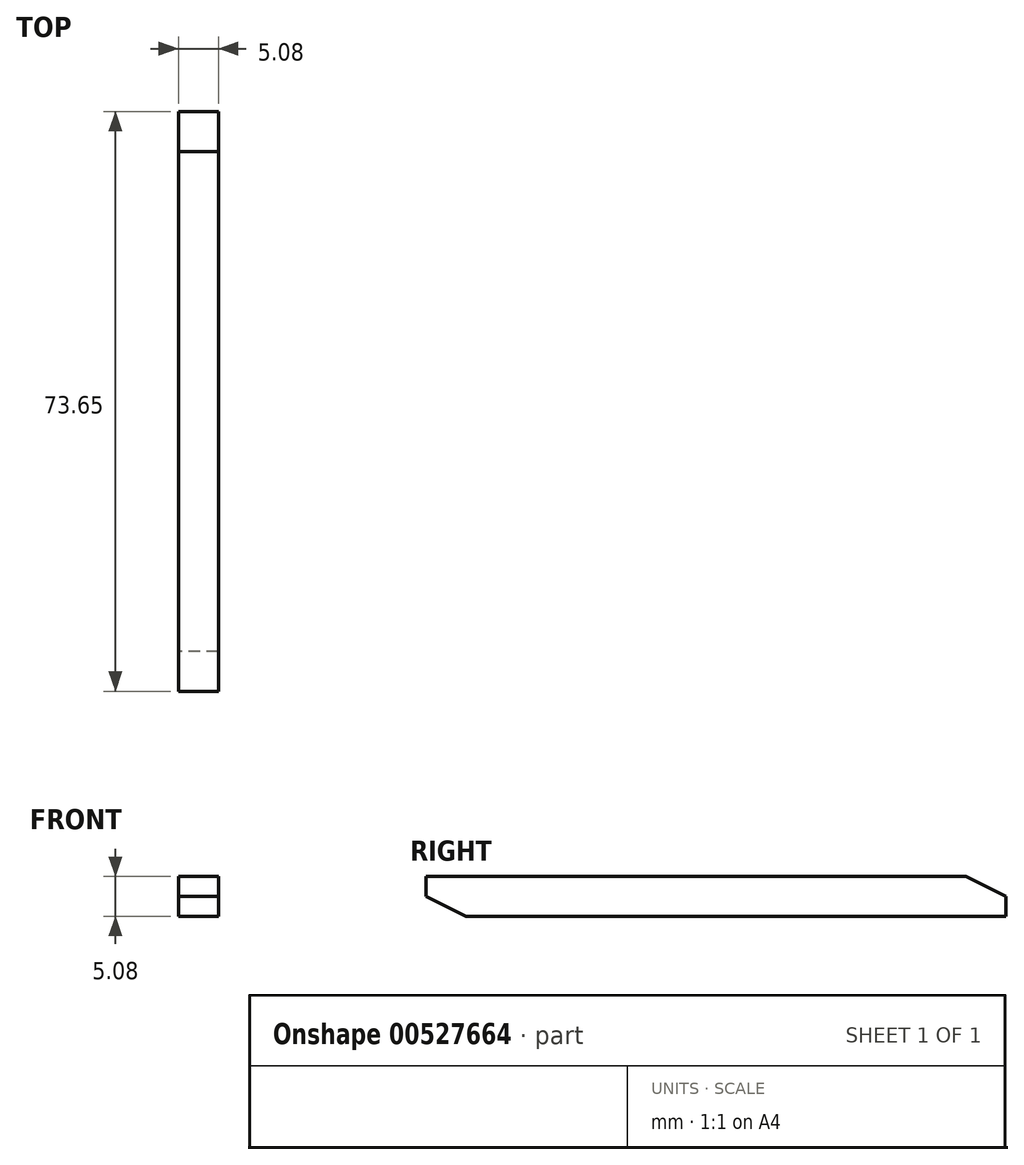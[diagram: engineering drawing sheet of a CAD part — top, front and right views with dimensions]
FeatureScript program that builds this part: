
annotation { "Feature Type Name" : "Feature", "Feature Type Description" : "" }
export const myFeature = defineFeature(function(context is Context, id is Id, definition is map)
    precondition{}
    {
        {
            var Q0;
            Q0=qCreatedBy(makeId("Right.planeOp"),FACE);
            var sketch = newSketch(context, id + "F0", { "sketchPlane" : qUnion([Q0])});
            skLineSegment(sketch, "E0.bottom", {"start": v(-23.9, 3.95) * mm, "end": v(39.6, 3.95) * mm});
            skLineSegment(sketch, "E0.top", {"start": v(-23.9, 9.03) * mm, "end": v(39.6, 9.03) * mm});
            skLineSegment(sketch, "E0.left", {"start": v(-23.9, 3.95) * mm, "end": v(-23.9, 9.03) * mm});
            skLineSegment(sketch, "E0.right", {"start": v(39.6, 3.95) * mm, "end": v(39.6, 9.03) * mm});
            skCircle(sketch, "E1.cCircle", {"center": v(-23.9, 6.5) * mm, "radius": 2.54 * mm, "construction": true});
            skLineSegment(sketch, "E1.0", {"start": v(-23.9, 3.95) * mm, "end": v(-26.44, 6.5) * mm});
            skLineSegment(sketch, "E1.1", {"start": v(-26.44, 6.5) * mm, "end": v(-23.9, 9.03) * mm});
            skLineSegment(sketch, "E1.2", {"start": v(-23.9, 9.03) * mm, "end": v(-21.36, 6.5) * mm});
            skLineSegment(sketch, "E1.3", {"start": v(-21.36, 6.5) * mm, "end": v(-23.9, 3.95) * mm});
            skLineSegment(sketch, "E2.bottom", {"start": v(-23.9, 9.03) * mm, "end": v(-28.98, 9.03) * mm});
            skLineSegment(sketch, "E2.top", {"start": v(-23.9, 6.5) * mm, "end": v(-28.98, 6.5) * mm});
            skLineSegment(sketch, "E2.left", {"start": v(-23.9, 9.03) * mm, "end": v(-23.9, 6.5) * mm});
            skLineSegment(sketch, "E2.right", {"start": v(-28.98, 9.03) * mm, "end": v(-28.98, 6.5) * mm});
            skLineSegment(sketch, "E3", {"start": v(-28.98, 6.5) * mm, "end": v(-23.9, 3.95) * mm});
            skLineSegment(sketch, "E4.bottom", {"start": v(39.6, 9.03) * mm, "end": v(39.6, 9.03) * mm});
            skLineSegment(sketch, "E4.top", {"start": v(39.6, 6.5) * mm, "end": v(39.6, 6.5) * mm});
            skLineSegment(sketch, "E4.left", {"start": v(39.6, 9.03) * mm, "end": v(39.6, 6.5) * mm});
            skLineSegment(sketch, "E4.right", {"start": v(39.6, 9.03) * mm, "end": v(39.6, 6.5) * mm});
            skLineSegment(sketch, "E5.bottom", {"start": v(39.6, 6.5) * mm, "end": v(44.67, 6.5) * mm});
            skLineSegment(sketch, "E5.left", {"start": v(39.6, 6.5) * mm, "end": v(39.6, 9.03) * mm});
            skLineSegment(sketch, "E6.bottom", {"start": v(44.67, 6.5) * mm, "end": v(39.6, 6.5) * mm});
            skLineSegment(sketch, "E6.top", {"start": v(44.67, 3.95) * mm, "end": v(39.6, 3.95) * mm});
            skLineSegment(sketch, "E6.left", {"start": v(44.67, 6.5) * mm, "end": v(44.67, 3.95) * mm});
            skLineSegment(sketch, "E6.right", {"start": v(39.6, 6.5) * mm, "end": v(39.6, 3.95) * mm});
            skLineSegment(sketch, "E7", {"start": v(44.67, 6.5) * mm, "end": v(39.6, 9.03) * mm});
            skSolve(sketch);
        }
        {
            var Q0;
            Q0 = qSketchRegion(id + "F0", true);
            extrude(context, id + "F1", {"entities" : qUnion([Q0]), "depth" : 5.08 * mm, "offsetDistance" : 25.4 * mm});
        }
        {
            var Q0;
            Q0 = qSketchRegion(id + "F0", true);
            extrude(context, id + "F2", {"entities" : qUnion([Q0]), "operationType" : NewBodyOperationType.ADD, "depth" : 5.08 * mm, "offsetDistance" : 25.4 * mm});
        }
    });
